# Revit family: PRD_FrankeWS_UrnlFlshngVlvs_SelfClosingUrinalFlushValve_AQRM464
name_source: partatom
category: Plumbing Fixtures
revit_build: Autodesk Revit 2018 (Build: 20190510_1515(x64)
units: mm (PartAtom-declared; Revit-internal decimal feet)

## family parameters
Always vertical = Yes
Cut with Voids When Loaded = No
OmniClass Number = 23.45.05.14.99
OmniClass Title = Other Sanitary Washing Plumbing Fixtures
Part Type = Normal
Room Calculation Point = No
Round Connector Dimension = Use Diameter
Shared = No
Work Plane-Based = Yes

## types (1)
- AQRM464
    AssetType = Fixed
    BIMObjectName = PRD_AR_UrinalFlushingValves_SelfClosingUrinalFlushValve_AQRM464
    CalculationFlowRateColdWater = 0.30 liter per second
    Category = Pr_40_20_93_79, Urinal flushing valves
    Default Elevation = 1219 mm
    Description = AQUALINE urinal flush valve DN 15 for surface installation, flushing quantity and volume flow adjustable, with lockable water quantity regulator, inlet pipe and connector. All-metal construction polished chromium-plated brass.
    DiameterNominal = 15  [stored 0.0492126 ft]
    DurationUnit = year
    Features = all-metal construction polished chromium-plated brass
    Finish = chromed
    FlowColdWater = 0.3 L/s
    FlushValveMaterial = PRD_AR_ChromatedBrass_HighPolished
    FlushingRate = 0.7 L/s
    FunctionalPrinciple = Hydraulic self-closing
    GrossWeight = 0.90 kg
    HasIntegralShutOffDevice = Yes
    IfcExportAs = IfcValveType
    IfcExportType = FLUSHING
    InletSize = G 1/2 B
    IsHighPressure = No
    Manufacturer = KWC Group AG
    ManufacturerName = KWC Group AG
    ManufacturerURL = www.kwc.com
    Material = brass
    MaximumFlowPressure = 4.00 bar
    MaximumFlushWaterVolume = 4.00 liter
    MaximumFlushingFlow = 0.70 liter per second
    MinimumFlowPressure = 1.00 bar
    MinimumFlushWaterVolume = 2.00 liter
    MinimumFlushingFlow = 0.30 liter per second
    Model = AQRM464
    ModelNumber = 2000100071
    ModelReference = AQRM464
    NBSDescription = Urinal flushing valves
    NBSReference = 45-35-70/355
    Name = Urinal flush valve AQRM464
    NetWeight = 0.82 kg
    NominalDepth = 0 mm  [stored 0 ft]
    NominalHeight = 0 mm  [stored 0 ft]
    NominalWidth = 0 mm  [stored 0 ft]
    OutletSize = DN 15
    ProductInformation = https://pim.kwc.com
    ProtectiveShutdown = No
    SoundInsulation = 2
    SurfaceFinishFitting = Chromed
    TailorMade = No
    TypeOfFlushingFitting = Urinal flush valve
    TypeOfMounting = Wall mounting
    TypeOfOperation = Manual operation
    URL = www.kwc.com
    Uniclass2015Code = Pr_40_20_93_79
    Uniclass2015Title = Urinal flushing valves
    Uniclass2015Version = Products v1.17
    Version = 1
    WarrantyDurationUnit = year

note: [stored X ft] marks values corroborated as IEEE doubles in the binary element streams (Revit-internal decimal feet)

## geometry (parser evidence)
native form markers: Sweep x3
no freeform markers — native parametric forms only
